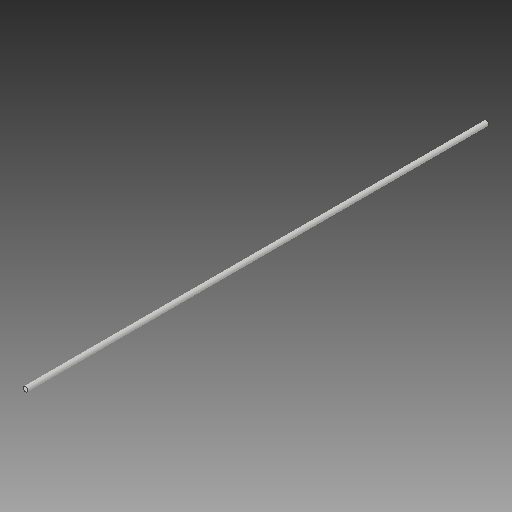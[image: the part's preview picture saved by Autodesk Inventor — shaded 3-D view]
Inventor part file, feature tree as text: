
AUTODESK INVENTOR PART (.ipt)
format: ipt  version: 2017 (Build 210142000, 142)  size: 87,040 bytes
history: native  units: in
note: dims shown in document units (in); Inventor stores cm internally (conversion verified against a paired STEP export)
features: extrude x1, sketch x1
ambient origin geometry x8: Origin, YZ Plane, XZ Plane, XY Plane, X Axis, Y Axis, Z Axis, Center Point
bodies: Solid1 (feature_tree)
feature tree (2):
  extrude  "Extrusion1"  Depth=12.0in TaperAngle=0.0deg
  sketch  "Sketch1"  dims[d0=0.125in d1=12.0in d2=0.0in]
